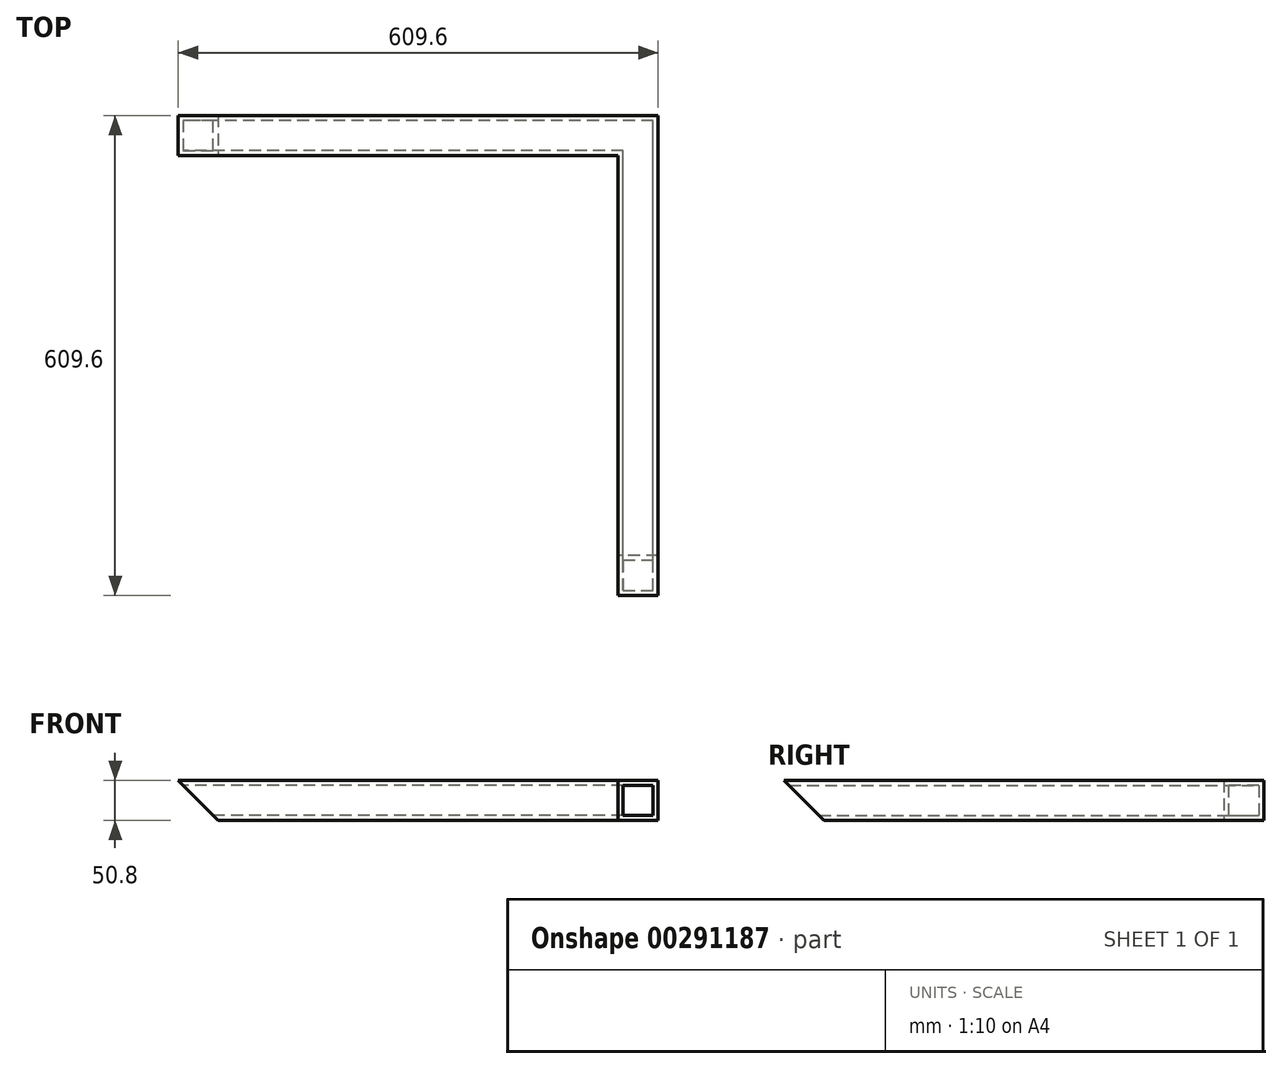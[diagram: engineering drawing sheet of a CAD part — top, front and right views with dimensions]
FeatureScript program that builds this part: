
annotation { "Feature Type Name" : "Feature", "Feature Type Description" : "" }
export const myFeature = defineFeature(function(context is Context, id is Id, definition is map)
    precondition{}
    {
        {
            var Q0;
            Q0=qCreatedBy(makeId("Top.planeOp"),FACE);
            var sketch = newSketch(context, id + "F0", { "sketchPlane" : qUnion([Q0])});
            skLineSegment(sketch, "E0", {"start": v(0, 0) * mm, "end": v(0, 584.2) * mm});
            skLineSegment(sketch, "E1", {"start": v(0, 584.2) * mm, "end": v(-584.2, 584.2) * mm});
            skSolve(sketch);
        }
        {
            var Q0;
            Q0=qCreatedBy(makeId("Front.planeOp"),FACE);
            var sketch = newSketch(context, id + "F1", { "sketchPlane" : qUnion([Q0])});
            skLineSegment(sketch, "E2.bottom", {"start": v(25.4, -25.4) * mm, "end": v(-25.4, -25.4) * mm});
            skLineSegment(sketch, "E2.top", {"start": v(25.4, 25.4) * mm, "end": v(-25.4, 25.4) * mm});
            skLineSegment(sketch, "E2.left", {"start": v(25.4, -25.4) * mm, "end": v(25.4, 25.4) * mm});
            skLineSegment(sketch, "E2.right", {"start": v(-25.4, -25.4) * mm, "end": v(-25.4, 25.4) * mm});
            skPoint(sketch, "E2.middle", {"position": v(0, 0) * mm});
            skLineSegment(sketch, "E3.0", {"start": v(19.05, 19.05) * mm, "end": v(-19.05, 19.05) * mm});
            skLineSegment(sketch, "E3.1", {"start": v(19.05, -19.05) * mm, "end": v(19.05, 19.05) * mm});
            skLineSegment(sketch, "E3.2", {"start": v(19.05, -19.05) * mm, "end": v(-19.05, -19.05) * mm});
            skLineSegment(sketch, "E3.3", {"start": v(-19.05, -19.05) * mm, "end": v(-19.05, 19.05) * mm});
            skSolve(sketch);
        }
        {
            var Q0;
            Q0=qSketchRegion(id+"F1",true);
            var Q1;
            Q1=qConstructionFilter(qBodyType(qCreatedBy(id+"F0",EDGE),BodyType.WIRE),ConstructionObject.NO);
            sweep(context, id + "F2", {"profiles" : qUnion([Q0]), "path" : qUnion([Q1])});
        }
        {
            var Q0;
            Q0=makeQuery(id+"F2.opSweep","SWEPT_FACE",FACE,{"disambiguationData":[OSD([sQuery(id+"F0.wireOp",EDGE,"E0"),sQuery(id+"F1.wireOp",EDGE,"E2.right")])]});
            var sketch = newSketch(context, id + "F3", { "sketchPlane" : qUnion([Q0])});
            skLineSegment(sketch, "E4", {"start": v(0, 25.4) * mm, "end": v(-50.8, -25.4) * mm});
            skLineSegment(sketch, "E5", {"start": v(-50.8, -25.4) * mm, "end": v(0, -25.4) * mm});
            skLineSegment(sketch, "E6", {"start": v(0, -25.4) * mm, "end": v(0, 25.4) * mm});
            skSolve(sketch);
        }
        {
            var Q0;
            Q0 = qSketchRegion(id + "F3", true);
            extrude(context, id + "F4", {"entities" : qUnion([Q0]), "operationType" : NewBodyOperationType.REMOVE, "endBound" : BoundingType.THROUGH_ALL, "oppositeDirection" : true, "depth" : 25.4 * mm});
        }
        {
            var Q0;
            Q0=makeQuery(id+"F2.opSweep","SWEPT_FACE",FACE,{"disambiguationData":[OSD([sQuery(id+"F0.wireOp",EDGE,"E1"),sQuery(id+"F1.wireOp",EDGE,"E2.right")])]});
            var sketch = newSketch(context, id + "F5", { "sketchPlane" : qUnion([Q0])});
            skLineSegment(sketch, "E7", {"start": v(-584.2, -25.4) * mm, "end": v(-533.4, -25.4) * mm});
            skLineSegment(sketch, "E8", {"start": v(-533.4, -25.4) * mm, "end": v(-584.2, 25.4) * mm});
            skLineSegment(sketch, "E9", {"start": v(-584.2, 25.4) * mm, "end": v(-584.2, -25.4) * mm});
            skSolve(sketch);
        }
        {
            var Q0;
            Q0 = qSketchRegion(id + "F5", true);
            extrude(context, id + "F6", {"entities" : qUnion([Q0]), "operationType" : NewBodyOperationType.REMOVE, "endBound" : BoundingType.THROUGH_ALL, "oppositeDirection" : true, "depth" : 25.4 * mm});
        }
    });
